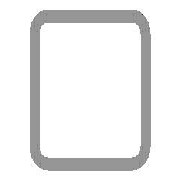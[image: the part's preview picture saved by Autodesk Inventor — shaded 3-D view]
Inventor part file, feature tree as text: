
AUTODESK INVENTOR PART (.ipt)
format: ipt  version: 2021 (Build 250183000, 183)  size: 289,792 bytes
history: native  units: mm (DEFAULTED — no unit token found)
features: other x5, sketch x5, extrude x3, pattern_linear x2, plane x1
ambient origin geometry x8: Origin, YZ Plane, XZ Plane, XY Plane, X Axis, Y Axis, Z Axis, Center Point
bodies: Solid1 (feature_tree)
feature tree (16):
  other  "Driven Length"
  other  "Płaszczyzna początkowa"
  other  "Płaszczyzna końcowa"
  extrude  "Bryła"  TaperAngle=0.0deg  [1 undecoded]
  extrude  "Wyciągnięcie proste2"  Depth=25.0mm
  other  "Oś konstrukcyjna1"
  other  "Oś konstrukcyjna2"
  pattern_linear  "Szyk prostokątny1"  Spacing1=25.0mm  [1 undecoded]
  extrude  "Wyciągnięcie proste3"  Depth=2.5mm
  pattern_linear  "Szyk prostokątny2"  Spacing1=-0.0mm  [1 undecoded]
  sketch  "Szkic"
  sketch  "Sketch3"  dims[d3=2000.0mm d4=0.0mm]
  plane  "Work Plane3"
  sketch  "Sketch4"  dims[d7=5.0mm d9=25.0mm d11=25.0mm d12=2.5mm d13=-0.0mm d14=2000.0mm d15=12.5mm d16=12.5mm d17=90.0deg d18=2000.0mm d19=6.0mm d20=25.0mm d21=10.0mm d22=0.0mm d23=780.0mm d25=25.0mm d26=3.0mm d27=10.0mm d28=0.0mm d29=760.0mm d31=25.0mm]
  sketch  "Szkic5"
  sketch  "Szkic6"
note: 3 required parameter values undecoded (feature->parameter linkage not recoverable at this tier; creation-order binding heuristic only, values carry confidence <= 0.55)
